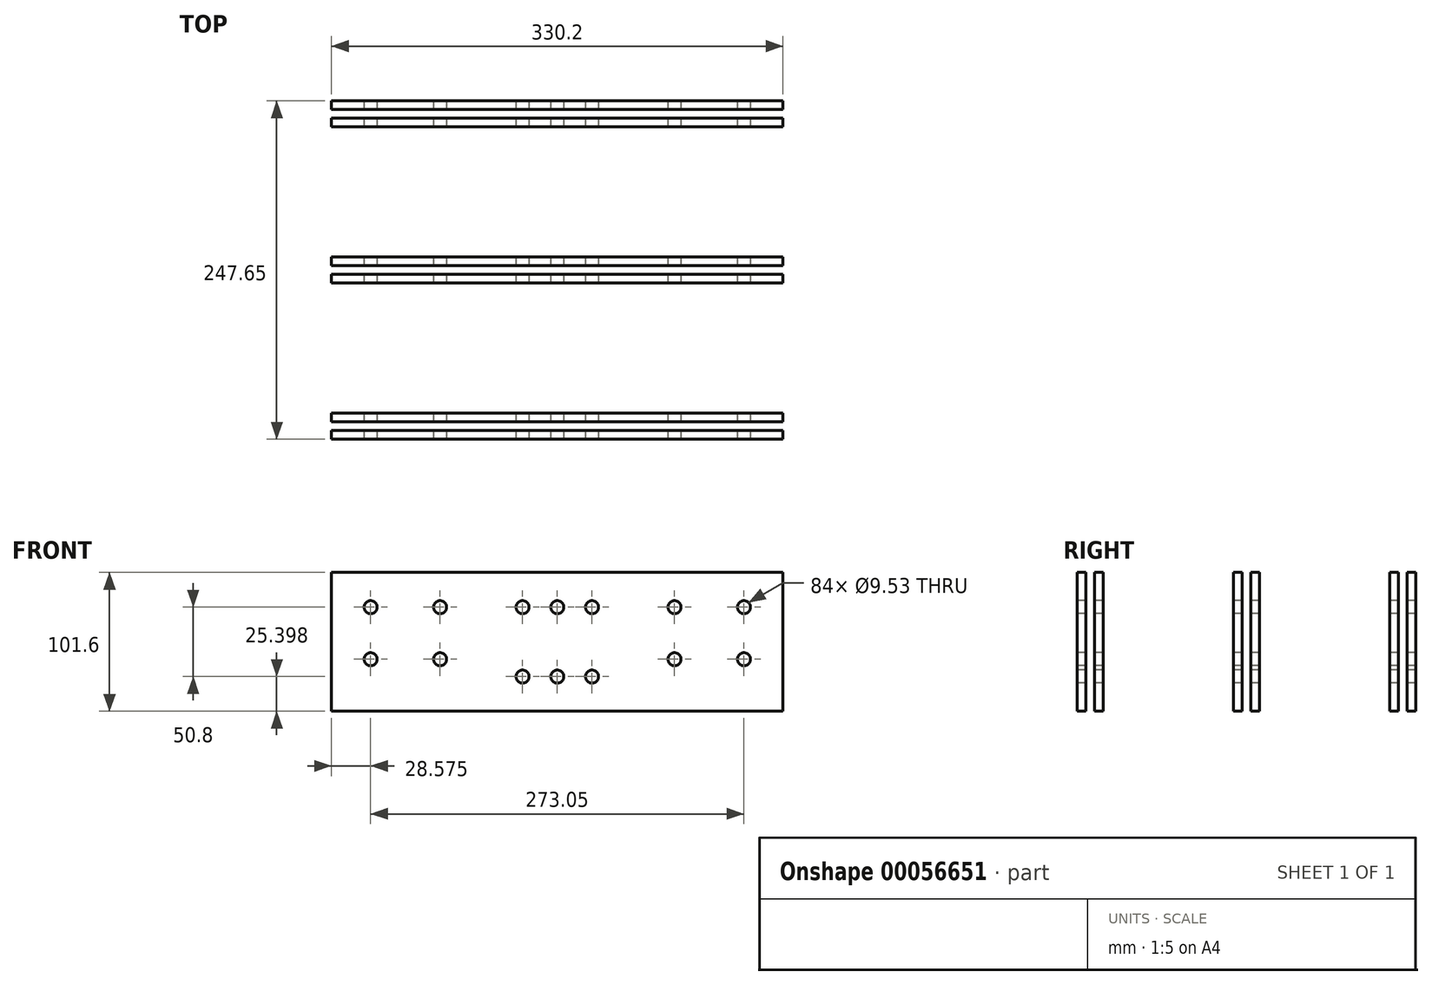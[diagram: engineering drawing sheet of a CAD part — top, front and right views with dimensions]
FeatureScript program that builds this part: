
annotation { "Feature Type Name" : "Feature", "Feature Type Description" : "" }
export const myFeature = defineFeature(function(context is Context, id is Id, definition is map)
    precondition{}
    {
        {
            var Q0;
            Q0=qCreatedBy(makeId("Right.planeOp"),FACE);
            var sketch = newSketch(context, id + "F0", { "sketchPlane" : qUnion([Q0])});
            skLineSegment(sketch, "E0.bottom", {"start": v(-60.03, 76.53) * mm, "end": v(-53.68, 76.53) * mm});
            skLineSegment(sketch, "E0.top", {"start": v(-60.03, -25.07) * mm, "end": v(-53.68, -25.07) * mm});
            skLineSegment(sketch, "E0.left", {"start": v(-60.03, 76.53) * mm, "end": v(-60.03, -25.07) * mm});
            skLineSegment(sketch, "E0.right", {"start": v(-53.68, 76.53) * mm, "end": v(-53.68, -25.07) * mm});
            skLineSegment(sketch, "E1.bottom", {"start": v(-47.33, 76.53) * mm, "end": v(-40.98, 76.53) * mm});
            skLineSegment(sketch, "E1.top", {"start": v(-47.33, -25.07) * mm, "end": v(-40.98, -25.07) * mm});
            skLineSegment(sketch, "E1.left", {"start": v(-47.33, 76.53) * mm, "end": v(-47.33, -25.07) * mm});
            skLineSegment(sketch, "E1.right", {"start": v(-40.98, 76.53) * mm, "end": v(-40.98, -25.07) * mm});
            skLineSegment(sketch, "E2.1.0.0", {"start": v(73.32, 76.53) * mm, "end": v(73.32, -25.07) * mm});
            skLineSegment(sketch, "E2.1.0.1", {"start": v(66.97, 76.53) * mm, "end": v(66.97, -25.07) * mm});
            skLineSegment(sketch, "E2.1.0.2", {"start": v(66.97, -25.07) * mm, "end": v(73.32, -25.07) * mm});
            skLineSegment(sketch, "E2.1.0.3", {"start": v(66.97, 76.53) * mm, "end": v(73.32, 76.53) * mm});
            skLineSegment(sketch, "E2.1.0.4", {"start": v(60.62, 76.53) * mm, "end": v(60.62, -25.07) * mm});
            skLineSegment(sketch, "E2.1.0.5", {"start": v(54.27, 76.53) * mm, "end": v(54.27, -25.07) * mm});
            skLineSegment(sketch, "E2.1.0.6", {"start": v(54.27, -25.07) * mm, "end": v(60.62, -25.07) * mm});
            skLineSegment(sketch, "E2.1.0.7", {"start": v(54.27, 76.53) * mm, "end": v(60.62, 76.53) * mm});
            skLineSegment(sketch, "E2.2.0.0", {"start": v(187.62, 76.53) * mm, "end": v(187.62, -25.07) * mm});
            skLineSegment(sketch, "E2.2.0.1", {"start": v(181.27, 76.53) * mm, "end": v(181.27, -25.07) * mm});
            skLineSegment(sketch, "E2.2.0.2", {"start": v(181.27, -25.07) * mm, "end": v(187.62, -25.07) * mm});
            skLineSegment(sketch, "E2.2.0.3", {"start": v(181.27, 76.53) * mm, "end": v(187.62, 76.53) * mm});
            skLineSegment(sketch, "E2.2.0.4", {"start": v(174.92, 76.53) * mm, "end": v(174.92, -25.07) * mm});
            skLineSegment(sketch, "E2.2.0.5", {"start": v(168.57, 76.53) * mm, "end": v(168.57, -25.07) * mm});
            skLineSegment(sketch, "E2.2.0.6", {"start": v(168.57, -25.07) * mm, "end": v(174.92, -25.07) * mm});
            skLineSegment(sketch, "E2.2.0.7", {"start": v(168.57, 76.53) * mm, "end": v(174.92, 76.53) * mm});
            skLineSegment(sketch, "E2.direction1", {"start": v(-40.98, -25.07) * mm, "end": v(73.32, -25.07) * mm, "construction": true});
            skSolve(sketch);
        }
        {
            var Q0;
            Q0 = qSketchRegion(id + "F0", true);
            extrude(context, id + "F1", {"entities" : qUnion([Q0]), "endBound" : BoundingType.SYMMETRIC, "depth" : 330.2 * mm});
        }
        {
            var Q0;
            Q0=makeQuery(id+"F1.opExtrude","SWEPT_FACE",FACE,{"disambiguationData":[OSD([sQuery(id+"F0.wireOp",EDGE,"E0.left")])]});
            var sketch = newSketch(context, id + "F2", { "sketchPlane" : qUnion([Q0])});
            skCircle(sketch, "E3", {"center": v(-136.53, 51.13) * mm, "radius": 4.76 * mm});
            skCircle(sketch, "E4", {"center": v(136.53, 51.13) * mm, "radius": 4.76 * mm});
            skCircle(sketch, "E5", {"center": v(-25.4, 0.33) * mm, "radius": 4.76 * mm});
            skCircle(sketch, "E6.0.1.0", {"center": v(-136.53, 13.03) * mm, "radius": 4.76 * mm});
            skCircle(sketch, "E6.1.0.0", {"center": v(-85.72, 51.13) * mm, "radius": 4.76 * mm});
            skCircle(sketch, "E6.1.1.0", {"center": v(-85.72, 13.03) * mm, "radius": 4.76 * mm});
            skLineSegment(sketch, "E6.direction1", {"start": v(-136.53, 51.13) * mm, "end": v(-85.72, 51.13) * mm, "construction": true});
            skLineSegment(sketch, "E6.direction2", {"start": v(-136.53, 51.13) * mm, "end": v(-136.53, 13.03) * mm, "construction": true});
            skCircle(sketch, "E7.0.1.0", {"center": v(136.53, 13.03) * mm, "radius": 4.76 * mm});
            skCircle(sketch, "E7.1.0.0", {"center": v(85.72, 51.13) * mm, "radius": 4.76 * mm});
            skCircle(sketch, "E7.1.1.0", {"center": v(85.72, 13.03) * mm, "radius": 4.76 * mm});
            skLineSegment(sketch, "E7.direction1", {"start": v(136.53, 51.13) * mm, "end": v(85.72, 51.13) * mm, "construction": true});
            skLineSegment(sketch, "E7.direction2", {"start": v(136.53, 51.13) * mm, "end": v(136.53, 13.03) * mm, "construction": true});
            skCircle(sketch, "E8.0.1.0", {"center": v(-25.4, 51.13) * mm, "radius": 4.76 * mm});
            skCircle(sketch, "E8.1.0.0", {"center": v(0, 0.33) * mm, "radius": 4.76 * mm});
            skCircle(sketch, "E8.1.1.0", {"center": v(0, 51.13) * mm, "radius": 4.76 * mm});
            skCircle(sketch, "E8.2.0.0", {"center": v(25.4, 0.33) * mm, "radius": 4.76 * mm});
            skCircle(sketch, "E8.2.1.0", {"center": v(25.4, 51.13) * mm, "radius": 4.76 * mm});
            skLineSegment(sketch, "E8.direction1", {"start": v(-25.4, 0.33) * mm, "end": v(0, 0.33) * mm, "construction": true});
            skLineSegment(sketch, "E8.direction2", {"start": v(-25.4, 0.33) * mm, "end": v(-25.4, 51.13) * mm, "construction": true});
            skSolve(sketch);
        }
        {
            var Q0;
            Q0 = qSketchRegion(id + "F2", true);
            extrude(context, id + "F3", {"entities" : qUnion([Q0]), "operationType" : NewBodyOperationType.REMOVE, "endBound" : BoundingType.THROUGH_ALL, "oppositeDirection" : true, "depth" : 25.4 * mm});
        }
    });
